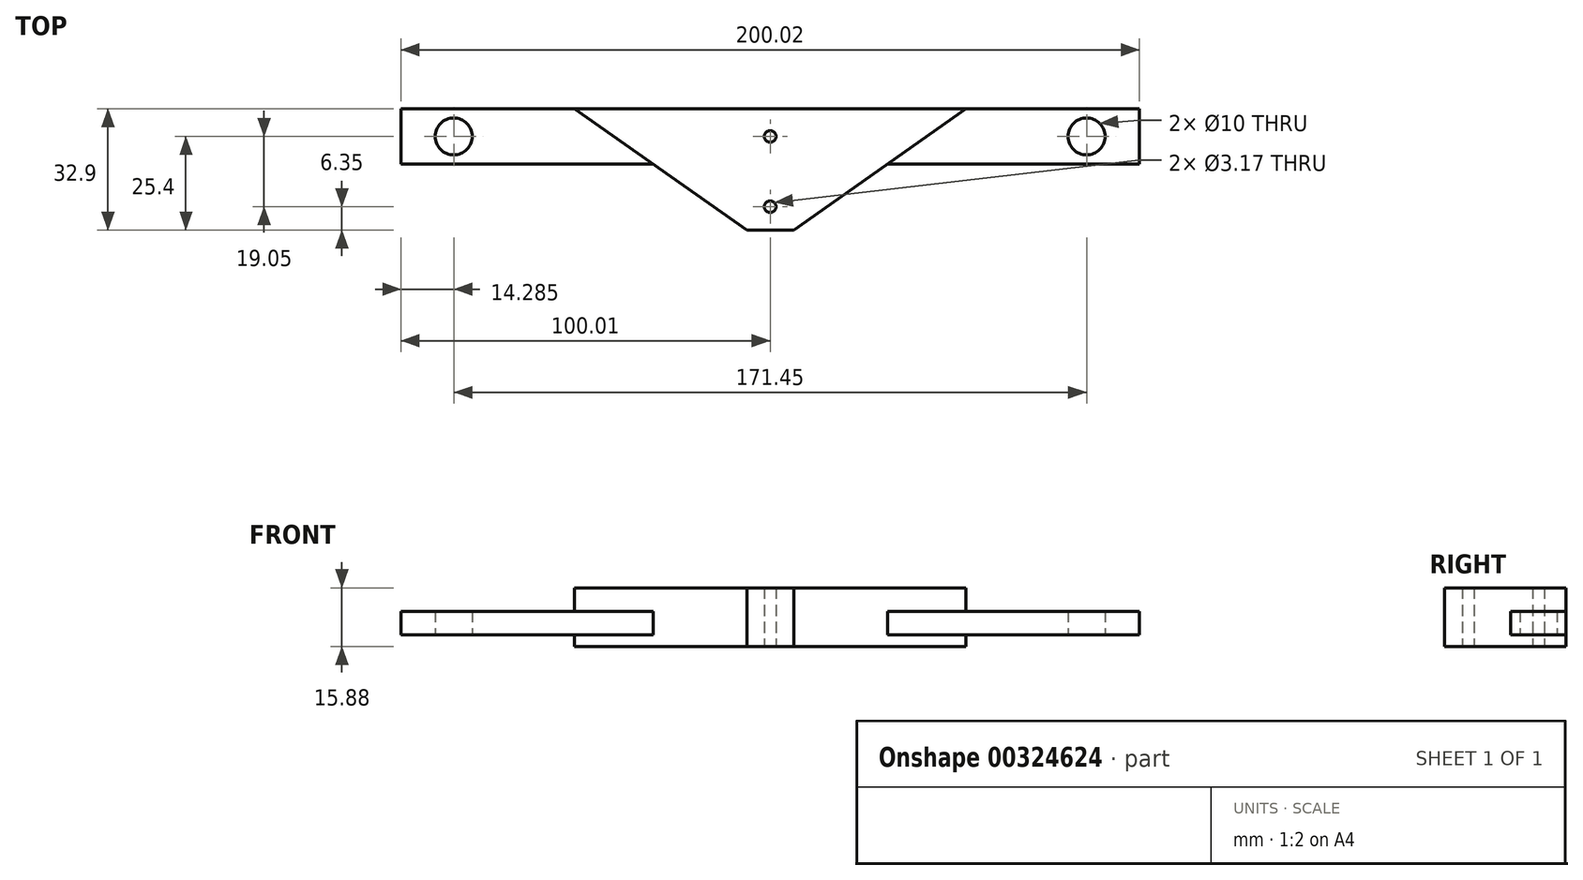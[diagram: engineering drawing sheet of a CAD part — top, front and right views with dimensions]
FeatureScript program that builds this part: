
annotation { "Feature Type Name" : "Feature", "Feature Type Description" : "" }
export const myFeature = defineFeature(function(context is Context, id is Id, definition is map)
    precondition{}
    {
        {
            var Q0;
            Q0=qCreatedBy(makeId("Top.planeOp"),FACE);
            var sketch = newSketch(context, id + "F0", { "sketchPlane" : qUnion([Q0])});
            skLineSegment(sketch, "E0.bottom", {"start": v(-100.01, 7.5) * mm, "end": v(100.01, 7.5) * mm});
            skLineSegment(sketch, "E0.top", {"start": v(-100.01, -7.5) * mm, "end": v(100.01, -7.5) * mm});
            skLineSegment(sketch, "E0.left", {"start": v(-100.01, 7.5) * mm, "end": v(-100.01, -7.5) * mm});
            skLineSegment(sketch, "E0.right", {"start": v(100.01, 7.5) * mm, "end": v(100.01, -7.5) * mm});
            skPoint(sketch, "E0.middle", {"position": v(0, 0) * mm});
            skCircle(sketch, "E1", {"center": v(0, -19.05) * mm, "radius": 1.59 * mm});
            skLineSegment(sketch, "E2", {"start": v(-31.75, -7.5) * mm, "end": v(-6.35, -25.4) * mm});
            skLineSegment(sketch, "E3", {"start": v(-6.35, -25.4) * mm, "end": v(6.35, -25.4) * mm});
            skLineSegment(sketch, "E4", {"start": v(6.35, -25.4) * mm, "end": v(31.75, -7.5) * mm});
            skPoint(sketch, "E5", {"position": v(0, -25.4) * mm});
            skLineSegment(sketch, "E6", {"start": v(-31.75, -7.5) * mm, "end": v(-53.03, 7.5) * mm});
            skLineSegment(sketch, "E7", {"start": v(31.75, -7.5) * mm, "end": v(53.03, 7.5) * mm});
            skCircle(sketch, "E8", {"center": v(85.72, 0) * mm, "radius": 5 * mm});
            skCircle(sketch, "E9.MirrorC", {"center": v(-85.72, 0) * mm, "radius": 5 * mm});
            skCircle(sketch, "E10", {"center": v(0, 0) * mm, "radius": 1.59 * mm});
            skSolve(sketch);
        }
        {
            var Q0;
            {var subQ1=sQuery(id+"F0.wireOp",EDGE,"E0.left");Q0=makeQuery(id+"F0.imprint","IMPRINT",FACE,{"disambiguationData":[TD([[makeQuery(id+"F0.imprint","IMPRINT",EDGE,{"derivedFrom":subQ1}),1.0]])]});}
            var Q1;
            {var subQ1=sQuery(id+"F0.wireOp",EDGE,"E0.right");Q1=makeQuery(id+"F0.imprint","IMPRINT",FACE,{"disambiguationData":[TD([[makeQuery(id+"F0.imprint","IMPRINT",EDGE,{"derivedFrom":subQ1}),-1.0]])]});}
            extrude(context, id + "F1", {"entities" : qUnion([Q0, Q1]), "depth" : 6.35 * mm});
        }
        {
            var Q0;
            {var subQ0=sQuery(id+"F0.wireOp",EDGE,"E6");Q0=makeQuery(id+"F0.imprint","IMPRINT",FACE,{"disambiguationData":[TD([[makeQuery(id+"F0.imprint","IMPRINT",EDGE,{"derivedFrom":subQ0}),-1.0]])]});}
            var Q1;
            Q1=makeQuery(id+"F0.imprint","IMPRINT",FACE,{"disambiguationData":[TD([[makeQuery(id+"F0.imprint","IMPRINT",EDGE,{"derivedFrom":sQuery(id+"F0.wireOp",EDGE,"E1")}),-1.0]])]});
            extrude(context, id + "F2", {"entities" : qUnion([Q0, Q1]), "operationType" : NewBodyOperationType.ADD, "depth" : 12.7 * mm, "hasSecondDirection" : true, "secondDirectionOppositeDirection" : true, "secondDirectionDepth" : 3.17 * mm});
        }
    });
